# Revit family: QF_RATIONAL_CombiSteamer_iCC_6-21E
name_source: partatom
category: Specialty Equipment
revit_build: Autodesk Revit 2018 (Build: 20170223_1515(x64)
units: mm (PartAtom-declared; Revit-internal decimal feet)

## family parameters
Always vertical = Yes
Cut with Voids When Loaded = No
OmniClass Number = 23.40.40.14.17.11
OmniClass Title = Cookers, Ovens, Stoves
Part Type = Normal
Room Calculation Point = No
Round Connector Dimension = Use Diameter
Shared = No
Work Plane-Based = No

## types (10) — shared parameters
Assembly Code = E1090320
Cold Water Flow = 0.2 L/s
Cold Water Maximum Pressure = 6.0 bar
Cold Water Minimum Pressure = 1.0 bar
Cold Water Size = 1"
Conn Conduit = Yes
Cycle = 50 Hz
Cycle Alternative = 60 Hz
Depth Actual = 38 1/2"
Description = Electrical Combi-steamer (6 x 2/1 GN / 12 x 1/1 GN)
Direct Waste Size = 2"
Height Actual = 30"
Hood Exhaust Hood = Hood : Exhaust Hood
Hood UltraVent = Hood : UltraVent
Hood UltraVent Plus = Hood : UltraVent Plus
Kit with Rollers = Accessories : Adjustable Rollers
Latent Heat Output = 1 kW
Length Actual = 42 1/2"
Manufacturer = RATIONAL AG
Model = iCombi Classic 6-2/1 E
Phase = 3
Sensitive Heat Output = 1 kW
Sound Level = 56dBA
Specification by Manufacturer = Hot-air steamer (combi-steamer mode) for most of the cooking methods used in commercial kitchens for the optional use of steam and hot-air, individually, in succession or in combination.
Stand Levelling Kit = Accessories : Levelling Kit
Stand None = Accessories : None
Stand UG I = Accessories : UG I 699
Stand UG I 200 = Accessories : UG I 200
Stand UG II = Accessories : UG II 699
Stand UG III = Accessories : UG III 699
Stand UG III Hood = Accessories : UG III 945
Stand UG IV = Accessories : UG IV 699
URL = www.rational-online.com
Version = 05-2020
Warranty Duration = 2 years
Waste Water Discharge Temperature = 65 °C
Weight = 137.00 kg

## per-type parameters (varying)
| type | FL Amps | Max Overcurrent Protection | Volts | Watts |
| 6-2/1E 3AC 220V | 54 A | 63 A | 220 V | 20600 W |
| 6-2/1E 3NAC 415V | 34 A | 35 A | 415 V | 24200 W |
| 6-2/1E 3NAC 400V | 32 A | 35 A | 400 V | 22400 W |
| 6-2/1E 3AC 480V | 27 A | 32 A | 480 V | 22400 W |
| 6-2/1E 3AC 440V | 29 A | 32 A | 440 V | 22400 W |
| 6-2/1E 3AC 400V | 32 A | 35 A | 400 V | 22400 W |
| 6-2/1E 3AC 240V | 59 A | 63 A | 240 V | 24300 W |
| 6-2/1E 3AC 230V | 56 A | 63 A | 230 V | 22400 W |
| 6-2/1E 3AC 208V | 62 A | 80 A | 208 V | 22400 W |
| 6-2/1E 3AC 200V | 60 A | 63 A | 200 V | 20800 W |

## geometry (parser evidence)
native form markers: Sweep x22
no freeform markers — native parametric forms only
